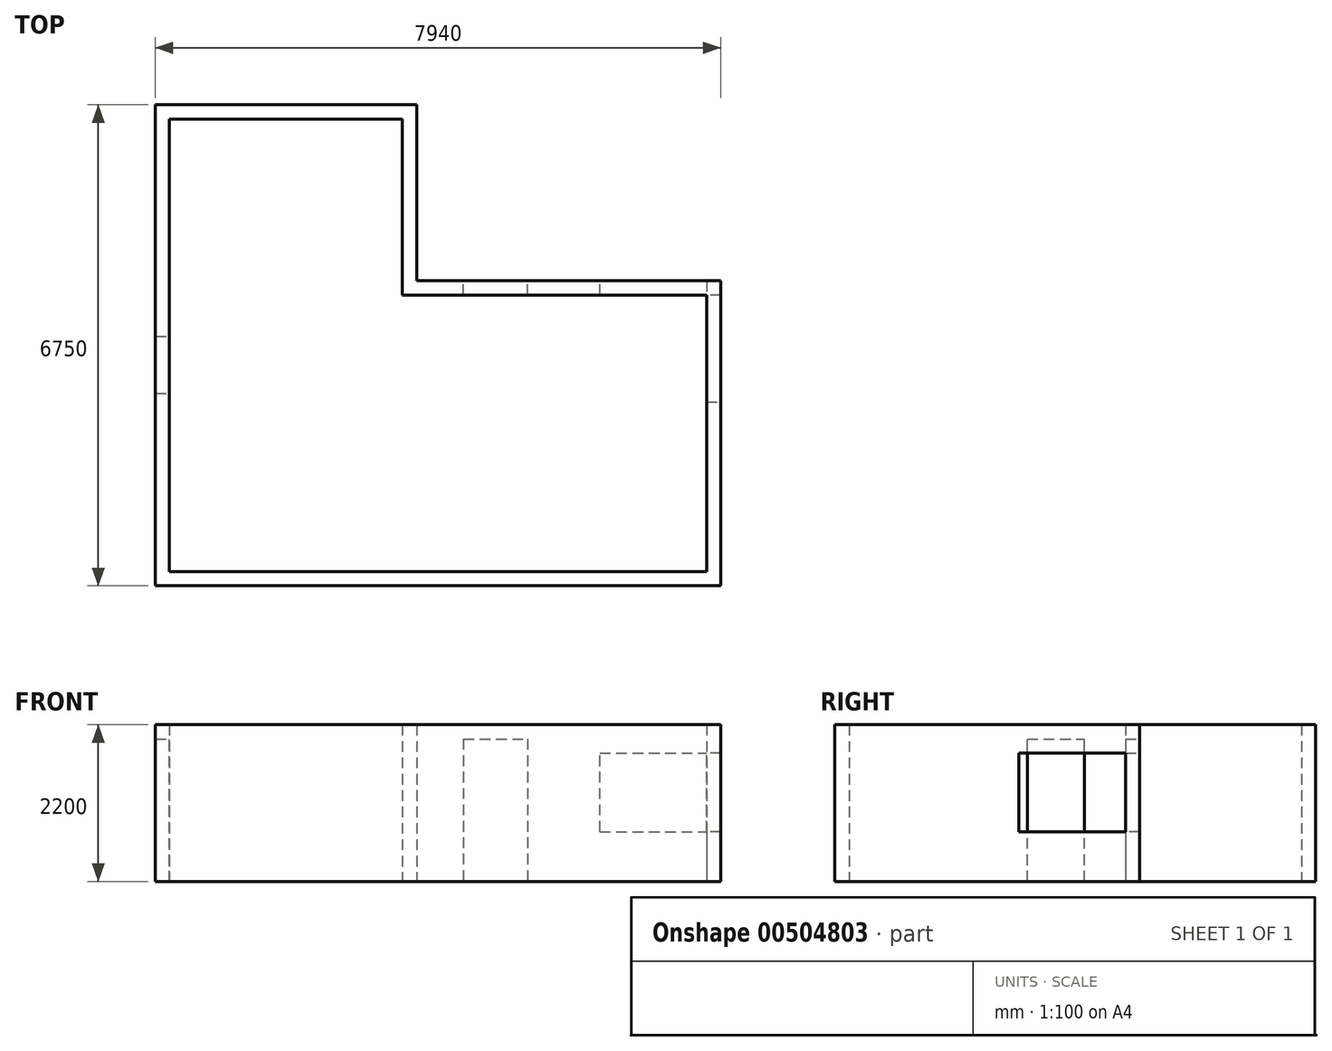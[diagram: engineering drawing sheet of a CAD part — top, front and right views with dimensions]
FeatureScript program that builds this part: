
annotation { "Feature Type Name" : "Feature", "Feature Type Description" : "" }
export const myFeature = defineFeature(function(context is Context, id is Id, definition is map)
    precondition{}
    {
        {
            var Q0;
            Q0=qCreatedBy(makeId("Top.planeOp"),FACE);
            var sketch = newSketch(context, id + "F0", { "sketchPlane" : qUnion([Q0])});
            skLineSegment(sketch, "E0.bottom", {"start": v(0, 0) * mm, "end": v(3670, 0) * mm});
            skLineSegment(sketch, "E0.top", {"start": v(0, -6750) * mm, "end": v(7940, -6750) * mm});
            skLineSegment(sketch, "E0.left", {"start": v(0, 0) * mm, "end": v(0, -6750) * mm});
            skLineSegment(sketch, "E0.right", {"start": v(7940, 0) * mm, "end": v(7940, -2470) * mm});
            skLineSegment(sketch, "E1.bottom", {"start": v(7940, 0) * mm, "end": v(3670, 0) * mm});
            skLineSegment(sketch, "E1.top", {"start": v(7940, -2470) * mm, "end": v(3670, -2470) * mm});
            skLineSegment(sketch, "E1.right", {"start": v(3670, 0) * mm, "end": v(3670, -2470) * mm});
            skLineSegment(sketch, "E2", {"start": v(7940, -2470) * mm, "end": v(7940, -6750) * mm});
            skLineSegment(sketch, "E3", {"start": v(3670, 0) * mm, "end": v(7940, 0) * mm});
            skLineSegment(sketch, "E4.0", {"start": v(7740, -2670) * mm, "end": v(3470, -2670) * mm});
            skLineSegment(sketch, "E4.1", {"start": v(200, -6550) * mm, "end": v(7740, -6550) * mm});
            skLineSegment(sketch, "E4.2", {"start": v(200, -200) * mm, "end": v(200, -6550) * mm});
            skLineSegment(sketch, "E4.3", {"start": v(7740, -2670) * mm, "end": v(7740, -6550) * mm});
            skLineSegment(sketch, "E4.4", {"start": v(200, -200) * mm, "end": v(3470, -200) * mm});
            skLineSegment(sketch, "E4.5", {"start": v(3470, -200) * mm, "end": v(3470, -2670) * mm});
            skPoint(sketch, "E5", {"position": v(5220, -2470) * mm});
            skPoint(sketch, "E6", {"position": v(200, -4050) * mm});
            skLineSegment(sketch, "E7", {"start": v(7940, -2470) * mm, "end": v(7940, -4170) * mm});
            skLineSegment(sketch, "E8", {"start": v(7940, -2470) * mm, "end": v(6240, -2470) * mm});
            skSolve(sketch);
        }
        {
            var Q0;
            Q0=makeQuery(id+"F0.imprint","IMPRINT",FACE,{"disambiguationData":[TD([[makeQuery(id+"F0.imprint","IMPRINT",EDGE,{"derivedFrom":sQuery(id+"F0.wireOp",EDGE,"E0.bottom")}),-1.0]])]});
            extrude(context, id + "F1", {"entities" : qUnion([Q0]), "depth" : 2200 * mm});
        }
        {
            var Q0;
            Q0=makeQuery(id+"F1.opExtrude","SWEPT_FACE",FACE,{"disambiguationData":[OSD([sQuery(id+"F0.wireOp",EDGE,"E1.top")])]});
            var sketch = newSketch(context, id + "F2", { "sketchPlane" : qUnion([Q0])});
            skLineSegment(sketch, "E9.bottom", {"start": v(-5224.97, 0) * mm, "end": v(-4324.97, 0) * mm});
            skLineSegment(sketch, "E9.top", {"start": v(-5224.97, 2000) * mm, "end": v(-4324.97, 2000) * mm});
            skLineSegment(sketch, "E9.left", {"start": v(-5224.97, 0) * mm, "end": v(-5224.97, 2000) * mm});
            skLineSegment(sketch, "E9.right", {"start": v(-4324.97, 0) * mm, "end": v(-4324.97, 2000) * mm});
            skPoint(sketch, "E10.0", {"position": v(-6240, 0) * mm});
            skLineSegment(sketch, "E11", {"start": v(-6240, 0) * mm, "end": v(-6240, 700) * mm});
            skLineSegment(sketch, "E12.bottom", {"start": v(-6240, 700) * mm, "end": v(-7940, 700) * mm});
            skLineSegment(sketch, "E12.top", {"start": v(-6240, 1800) * mm, "end": v(-7940, 1800) * mm});
            skLineSegment(sketch, "E12.left", {"start": v(-6240, 700) * mm, "end": v(-6240, 1800) * mm});
            skLineSegment(sketch, "E12.right", {"start": v(-7940, 700) * mm, "end": v(-7940, 1800) * mm});
            skSolve(sketch);
        }
        {
            var Q0;
            Q0=makeQuery(id+"F2.imprint","IMPRINT",FACE,{"disambiguationData":[TD([[makeQuery(id+"F2.imprint","IMPRINT",EDGE,{"derivedFrom":sQuery(id+"F2.wireOp",EDGE,"E9.bottom")}),1.0]])]});
            extrude(context, id + "F3", {"entities" : qUnion([Q0]), "operationType" : NewBodyOperationType.REMOVE, "oppositeDirection" : true, "depth" : 300 * mm});
        }
        {
            var Q0;
            Q0=makeQuery(id+"F1.opExtrude","SWEPT_FACE",FACE,{"disambiguationData":[OSD([sQuery(id+"F0.wireOp",EDGE,"E4.2")])]});
            var sketch = newSketch(context, id + "F4", { "sketchPlane" : qUnion([Q0])});
            skLineSegment(sketch, "E13.bottom", {"start": v(-4049.88, 0) * mm, "end": v(-3249.88, 0) * mm});
            skLineSegment(sketch, "E13.top", {"start": v(-4049.88, 2000) * mm, "end": v(-3249.88, 2000) * mm});
            skLineSegment(sketch, "E13.left", {"start": v(-4049.88, 0) * mm, "end": v(-4049.88, 2000) * mm});
            skLineSegment(sketch, "E13.right", {"start": v(-3249.88, 0) * mm, "end": v(-3249.88, 2000) * mm});
            skSolve(sketch);
        }
        {
            var Q0;
            Q0=makeQuery(id+"F4.imprint","IMPRINT",FACE,{"disambiguationData":[TD([[makeQuery(id+"F4.imprint","IMPRINT",EDGE,{"derivedFrom":sQuery(id+"F4.wireOp",EDGE,"E13.bottom")}),-1.0]])]});
            extrude(context, id + "F5", {"entities" : qUnion([Q0]), "operationType" : NewBodyOperationType.REMOVE, "oppositeDirection" : true, "depth" : 300 * mm});
        }
        {
            var Q0;
            Q0=makeQuery(id+"F2.imprint","IMPRINT",FACE,{"disambiguationData":[TD([[makeQuery(id+"F2.imprint","IMPRINT",EDGE,{"derivedFrom":sQuery(id+"F2.wireOp",EDGE,"E12.bottom")}),-1.0]])]});
            extrude(context, id + "F6", {"entities" : qUnion([Q0]), "operationType" : NewBodyOperationType.REMOVE, "oppositeDirection" : true, "depth" : 200 * mm});
        }
        {
            var Q0;
            Q0=makeQuery(id+"F1.opExtrude","SWEPT_FACE",FACE,{"disambiguationData":[OSD([sQuery(id+"F0.wireOp",EDGE,"E2"),sQuery(id+"F0.wireOp",EDGE,"E7")])]});
            var sketch = newSketch(context, id + "F7", { "sketchPlane" : qUnion([Q0])});
            skPoint(sketch, "E14.0", {"position": v(-4170, 0) * mm});
            skLineSegment(sketch, "E15.bottom", {"start": v(-2470, 700) * mm, "end": v(-4170, 700) * mm});
            skLineSegment(sketch, "E15.top", {"start": v(-2470, 1800) * mm, "end": v(-4170, 1800) * mm});
            skLineSegment(sketch, "E15.left", {"start": v(-2470, 700) * mm, "end": v(-2470, 1800) * mm});
            skLineSegment(sketch, "E15.right", {"start": v(-4170, 700) * mm, "end": v(-4170, 1800) * mm});
            skSolve(sketch);
        }
        {
            var Q0;
            {var subQ2=sQuery(id+"F7.wireOp",EDGE,"E15.right");Q0=makeQuery(id+"F7.imprint","IMPRINT",FACE,{"disambiguationData":[TD([[makeQuery(id+"F7.imprint","IMPRINT",EDGE,{"derivedFrom":subQ2}),-1.0]])]});}
            extrude(context, id + "F8", {"entities" : qUnion([Q0]), "operationType" : NewBodyOperationType.REMOVE, "oppositeDirection" : true, "depth" : 200 * mm});
        }
        {
            var Q0;
            Q0=makeQuery(id+"F8.boolean.opBoolean","MERGE",FACE,{"derivedFrom":[makeQuery(id+"F6.boolean.opBoolean","COPY",FACE,{"derivedFrom":makeQuery(id+"F6.opExtrude","SWEPT_FACE",FACE,{"disambiguationData":[OSD([sQuery(id+"F2.wireOp",EDGE,"E12.bottom")])]})}),makeQuery(id+"F8.opExtrude","SWEPT_FACE",FACE,{"disambiguationData":[OSD([sQuery(id+"F7.wireOp",EDGE,"E15.bottom")])]})]});
            var sketch = newSketch(context, id + "F9", { "sketchPlane" : qUnion([Q0])});
            skLineSegment(sketch, "E16.bottom", {"start": v(7940, -2470) * mm, "end": v(7740, -2470) * mm});
            skLineSegment(sketch, "E16.top", {"start": v(7940, -2670) * mm, "end": v(7740, -2670) * mm});
            skLineSegment(sketch, "E16.left", {"start": v(7940, -2470) * mm, "end": v(7940, -2670) * mm});
            skLineSegment(sketch, "E16.right", {"start": v(7740, -2470) * mm, "end": v(7740, -2670) * mm});
            skSolve(sketch);
        }
        {
            var Q0;
            Q0=makeQuery(id+"F9.imprint","IMPRINT",FACE,{"disambiguationData":[TD([[makeQuery(id+"F9.imprint","IMPRINT",EDGE,{"derivedFrom":sQuery(id+"F9.wireOp",EDGE,"E16.bottom")}),-1.0]])]});
            extrude(context, id + "F10", {"entities" : qUnion([Q0]), "operationType" : NewBodyOperationType.ADD, "depth" : 1100 * mm});
        }
    });
